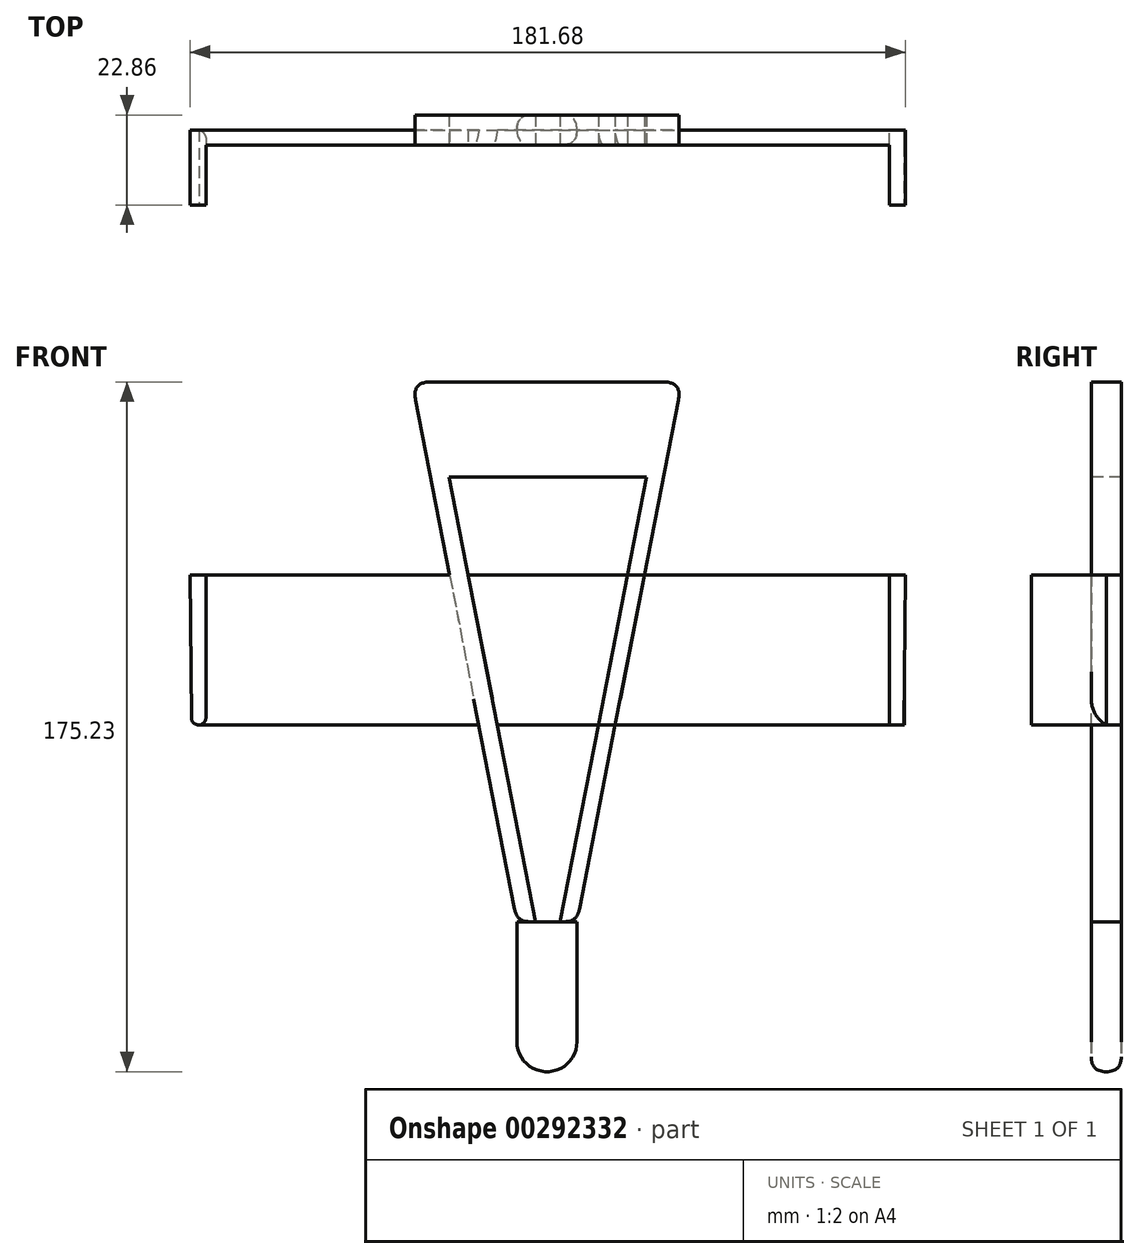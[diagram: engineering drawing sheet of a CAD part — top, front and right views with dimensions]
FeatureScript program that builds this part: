
annotation { "Feature Type Name" : "Feature", "Feature Type Description" : "" }
export const myFeature = defineFeature(function(context is Context, id is Id, definition is map)
    precondition{}
    {
        {
            var Q0;
            Q0=qCreatedBy(makeId("Front.planeOp"),FACE);
            var sketch = newSketch(context, id + "F0", { "sketchPlane" : qUnion([Q0])});
            skLineSegment(sketch, "E0", {"start": v(-7.81, -36.6) * mm, "end": v(7.43, -36.6) * mm});
            skLineSegment(sketch, "E1", {"start": v(7.43, -36.6) * mm, "end": v(7.43, -67.07) * mm});
            skLineSegment(sketch, "E2", {"start": v(-7.81, -36.6) * mm, "end": v(-7.81, -67.07) * mm});
            skArc(sketch, "E3", {"start": v(-7.81, -67.07) * mm, "mid": v(-0.2, -74.7) * mm, "end": v(7.43, -67.07) * mm});
            skLineSegment(sketch, "E4", {"start": v(7.43, -36.6) * mm, "end": v(34.07, 100.54) * mm});
            skLineSegment(sketch, "E5", {"start": v(34.07, 100.54) * mm, "end": v(-34.46, 100.54) * mm});
            skLineSegment(sketch, "E6", {"start": v(-34.46, 100.54) * mm, "end": v(-7.81, -36.6) * mm});
            skLineSegment(sketch, "E7", {"start": v(3.15, -36.6) * mm, "end": v(25.1, 76.38) * mm});
            skLineSegment(sketch, "E8", {"start": v(25.1, 76.38) * mm, "end": v(-25.04, 76.38) * mm});
            skLineSegment(sketch, "E9", {"start": v(-25.04, 76.38) * mm, "end": v(-3.1, -36.6) * mm});
            skLineSegment(sketch, "E10", {"start": v(-8.63, -8.1) * mm, "end": v(8.68, -8.1) * mm});
            skLineSegment(sketch, "E11", {"start": v(-11.11, 4.67) * mm, "end": v(11.16, 4.67) * mm});
            skLineSegment(sketch, "E12", {"start": v(-90.84, 51.55) * mm, "end": v(90.63, 51.55) * mm});
            skLineSegment(sketch, "E13", {"start": v(90.63, 51.55) * mm, "end": v(90.63, 13.38) * mm});
            skLineSegment(sketch, "E14", {"start": v(90.63, 13.38) * mm, "end": v(-90.52, 13.38) * mm});
            skLineSegment(sketch, "E15", {"start": v(-90.52, 13.38) * mm, "end": v(-90.84, 51.55) * mm});
            skSolve(sketch);
        }
        {
            var Q0;
            {var subQ0=sQuery(id+"F0.wireOp",EDGE,"E7");var subQ3=sQuery(id+"F0.wireOp",EDGE,"E0");var subQ4=makeQuery(id+"F0.imprint","INTERSECT",VERTEX,{"derivedFrom":[subQ3,subQ0]});Q0=makeQuery(id+"F0.imprint","IMPRINT",FACE,{"disambiguationData":[TD([[makeQuery(id+"F0.imprint","IMPRINT",EDGE,{"disambiguationData":[TD([[subQ4,-1.0]])],"derivedFrom":subQ0}),-1.0]])]});}
            var Q1;
            {var subQ5=sQuery(id+"F0.wireOp",EDGE,"E5");Q1=makeQuery(id+"F0.imprint","IMPRINT",FACE,{"disambiguationData":[TD([[makeQuery(id+"F0.imprint","IMPRINT",EDGE,{"derivedFrom":subQ5}),1.0]])]});}
            var Q2;
            {var subQ0=sQuery(id+"F0.wireOp",EDGE,"E9");var subQ1=makeQuery(id+"F0.imprint","INTERSECT",VERTEX,{"derivedFrom":[subQ0,sQuery(id+"F0.wireOp",EDGE,"E11")]});Q2=makeQuery(id+"F0.imprint","IMPRINT",FACE,{"disambiguationData":[TD([[makeQuery(id+"F0.imprint","IMPRINT",EDGE,{"disambiguationData":[TD([[subQ1,1.0]])],"derivedFrom":subQ0}),-1.0]])]});}
            extrude(context, id + "F1", {"entities" : qUnion([Q0, Q1, Q2]), "oppositeDirection" : true, "depth" : 7.62 * mm});
        }
        {
            var Q0;
            {var subQ0=sQuery(id+"F0.wireOp",EDGE,"E1");Q0=makeQuery(id+"F0.imprint","IMPRINT",FACE,{"disambiguationData":[TD([[makeQuery(id+"F0.imprint","IMPRINT",EDGE,{"derivedFrom":subQ0}),-1.0]])]});}
            extrude(context, id + "F2", {"entities" : qUnion([Q0]), "oppositeDirection" : true, "depth" : 7.62 * mm});
        }
        {
            var Q0;
            Q0=makeQuery(id+"F2.opExtrude","SWEPT_FACE",FACE,{"disambiguationData":[OSD([sQuery(id+"F0.wireOp",EDGE,"E3")])]});
            fillet(context, id + "F3", {"entities" : qUnion([Q0]), "radius" : 3.8 * mm, "tangentPropagation" : true, "rho" : 0.5, "crossSection" : FilletCrossSection.CONIC, "allowEdgeOverflow" : false});
        }
        {
            var Q0;
            {var subQ5=sQuery(id+"F0.wireOp",EDGE,"E13");Q0=makeQuery(id+"F0.imprint","IMPRINT",FACE,{"disambiguationData":[TD([[makeQuery(id+"F0.imprint","IMPRINT",EDGE,{"derivedFrom":subQ5}),-1.0]])]});}
            var Q1;
            {var subQ0=sQuery(id+"F0.wireOp",EDGE,"E14");var subQ1=sQuery(id+"F0.wireOp",EDGE,"E7");var subQ2=makeQuery(id+"F0.imprint","INTERSECT",VERTEX,{"derivedFrom":[subQ1,subQ0]});Q1=makeQuery(id+"F0.imprint","IMPRINT",FACE,{"disambiguationData":[TD([[makeQuery(id+"F0.imprint","IMPRINT",EDGE,{"disambiguationData":[TD([[subQ2,-1.0]])],"derivedFrom":subQ1}),1.0]])]});}
            var Q2;
            {var subQ5=sQuery(id+"F0.wireOp",EDGE,"E15");Q2=makeQuery(id+"F0.imprint","IMPRINT",FACE,{"disambiguationData":[TD([[makeQuery(id+"F0.imprint","IMPRINT",EDGE,{"derivedFrom":subQ5}),-1.0]])]});}
            extrude(context, id + "F4", {"entities" : qUnion([Q0, Q1, Q2]), "oppositeDirection" : true, "depth" : 3.8 * mm});
        }
        {
            var Q0;
            {var subQ0=sQuery(id+"F0.wireOp",EDGE,"E12");var subQ1=sQuery(id+"F0.wireOp",EDGE,"E6");var subQ2=makeQuery(id+"F0.imprint","INTERSECT",VERTEX,{"derivedFrom":[subQ1,subQ0]});Q0=makeQuery(id+"F0.imprint","IMPRINT",FACE,{"disambiguationData":[TD([[makeQuery(id+"F0.imprint","IMPRINT",EDGE,{"disambiguationData":[TD([[subQ2,-1.0]])],"derivedFrom":subQ1}),1.0]])]});}
            var Q1;
            {var subQ0=sQuery(id+"F0.wireOp",EDGE,"E14");var subQ1=sQuery(id+"F0.wireOp",EDGE,"E4");var subQ2=makeQuery(id+"F0.imprint","INTERSECT",VERTEX,{"derivedFrom":[subQ1,subQ0]});Q1=makeQuery(id+"F0.imprint","IMPRINT",FACE,{"disambiguationData":[TD([[makeQuery(id+"F0.imprint","IMPRINT",EDGE,{"disambiguationData":[TD([[subQ2,-1.0]])],"derivedFrom":subQ1}),1.0]])]});}
            extrude(context, id + "F5", {"entities" : qUnion([Q0, Q1]), "oppositeDirection" : true, "depth" : 7.62 * mm});
        }
        {
            var Q0;
            Q0=makeQuery(id+"F1.opExtrude","SWEPT_EDGE",EDGE,{"disambiguationData":[OSD([sQuery(id+"F0.wireOp",EDGE,"E4"),sQuery(id+"F0.wireOp",EDGE,"E5")])]});
            var Q1;
            Q1=makeQuery(id+"F1.opExtrude","SWEPT_EDGE",EDGE,{"disambiguationData":[OSD([sQuery(id+"F0.wireOp",EDGE,"E0"),sQuery(id+"F0.wireOp",EDGE,"E1"),sQuery(id+"F0.wireOp",EDGE,"E4")])]});
            var Q2;
            Q2=makeQuery(id+"F1.opExtrude","SWEPT_EDGE",EDGE,{"disambiguationData":[OSD([sQuery(id+"F0.wireOp",EDGE,"E0"),sQuery(id+"F0.wireOp",EDGE,"E2"),sQuery(id+"F0.wireOp",EDGE,"E6")])]});
            var Q3;
            Q3=makeQuery(id+"F1.opExtrude","SWEPT_EDGE",EDGE,{"disambiguationData":[OSD([sQuery(id+"F0.wireOp",EDGE,"E5"),sQuery(id+"F0.wireOp",EDGE,"E6")])]});
            fillet(context, id + "F6", {"entities" : qUnion([Q0, Q1, Q2, Q3]), "radius" : 3.8 * mm, "tangentPropagation" : true, "rho" : 0.5, "crossSection" : FilletCrossSection.CONIC, "allowEdgeOverflow" : false});
        }
        {
            var Q0;
            Q0=makeQuery(id+"F4.opExtrude","CAP_FACE",FACE,{"disambiguationData":[OSD([sQuery(id+"F0.wireOp",EDGE,"E6"),sQuery(id+"F0.wireOp",EDGE,"E12"),sQuery(id+"F0.wireOp",EDGE,"E14"),sQuery(id+"F0.wireOp",EDGE,"E15")])],"isStart":false});
            var sketch = newSketch(context, id + "F7", { "sketchPlane" : qUnion([Q0])});
            skLineSegment(sketch, "E16", {"start": v(86.83, 13.38) * mm, "end": v(86.83, 51.55) * mm});
            skLineSegment(sketch, "E17.MirrorCS", {"start": v(-86.83, 13.38) * mm, "end": v(-86.83, 51.55) * mm});
            skSolve(sketch);
        }
        {
            var Q0;
            {var subQ0=sQuery(id+"F7.wireOp",EDGE,"E16");Q0=makeQuery(id+"F7.imprint","IMPRINT",FACE,{"disambiguationData":[TD([[makeQuery(id+"F7.imprint","IMPRINT",EDGE,{"derivedFrom":subQ0}),-1.0]])]});}
            extrude(context, id + "F8", {"entities" : qUnion([Q0]), "operationType" : NewBodyOperationType.ADD, "oppositeDirection" : true, "depth" : 19.05 * mm});
        }
        {
            var Q0;
            Q0=makeQuery(id+"F4.opExtrude","SWEPT_BODY",BODY,{"disambiguationData":[OSD([sQuery(id+"F0.wireOp",EDGE,"E6"),sQuery(id+"F0.wireOp",EDGE,"E12"),sQuery(id+"F0.wireOp",EDGE,"E14"),sQuery(id+"F0.wireOp",EDGE,"E15")])]});
            var Q1;
            Q1=qCreatedBy(makeId("Right.planeOp"),FACE);
            mirror(context, id + "F9", {"operationType" : NewBodyOperationType.ADD, "entities" : qUnion([Q0]), "mirrorPlane" : qUnion([Q1])});
        }
        {
            var Q0;
            {var subQ0=sQuery(id+"F0.wireOp",EDGE,"E15");var subQ1=sQuery(id+"F0.wireOp",EDGE,"E14");Q0=makeQuery(id+"F8.boolean.opBoolean","MERGE",EDGE,{"derivedFrom":[makeQuery(id+"F4.opExtrude","SWEPT_EDGE",EDGE,{"disambiguationData":[OSD([subQ1,subQ0])]}),makeQuery(id+"F8.opExtrude","SWEPT_EDGE",EDGE,{"disambiguationData":[OSD([subQ1,subQ0])]})]});}
            fillet(context, id + "F10", {"entities" : qUnion([Q0]), "radius" : 1.9 * mm, "tangentPropagation" : true, "allowEdgeOverflow" : false});
        }
        {
            var Q0;
            Q0=makeQuery(id+"F8.opExtrude","SWEPT_EDGE",EDGE,{"disambiguationData":[OSD([sQuery(id+"F0.wireOp",EDGE,"E14"),sQuery(id+"F7.wireOp",EDGE,"E16")])]});
            fillet(context, id + "F11", {"entities" : qUnion([Q0]), "radius" : 1.9 * mm, "tangentPropagation" : true, "allowEdgeOverflow" : false});
        }
        {
            var Q0;
            {var subQ0=sQuery(id+"F0.wireOp",EDGE,"E14");Q0=makeQuery(id+"F4.opExtrude","CAP_EDGE",EDGE,{"disambiguationData":[OSD([subQ0]),TDD([makeQuery(id+"F0.imprint","IMPRINT",EDGE,{"disambiguationData":[TD([[makeQuery(id+"F0.imprint","INTERSECT",VERTEX,{"derivedFrom":[subQ0,sQuery(id+"F0.wireOp",EDGE,"E15")]}),1.0]])],"derivedFrom":subQ0})])],"isStart":true});}
            var Q1;
            {var subQ0=sQuery(id+"F0.wireOp",EDGE,"E14");var subQ1=sQuery(id+"F0.wireOp",EDGE,"E13");var subQ2=sQuery(id+"F0.wireOp",EDGE,"E4");var subQ3=makeQuery(id+"F4.opExtrude","CAP_FACE",FACE,{"disambiguationData":[OSD([subQ2,sQuery(id+"F0.wireOp",EDGE,"E12"),subQ1,subQ0])],"isStart":true});var subQ4=makeQuery(id+"F0.imprint","IMPRINT",EDGE,{"disambiguationData":[TD([[makeQuery(id+"F0.imprint","INTERSECT",VERTEX,{"derivedFrom":[subQ1,subQ0]}),-1.0]])],"derivedFrom":subQ0});var subQ5=makeQuery(id+"F4.opExtrude","SWEPT_FACE",FACE,{"disambiguationData":[OSD([subQ0]),TDD([subQ4])]});Q1=makeQuery(id+"F9.boolean.opBoolean","SPLIT",EDGE,{"disambiguationData":[topologyDisambiguationEdgeConnected([subQ3,subQ5]),TD([makeQuery(id+"F9.opPattern","COPY",FACE,{"derivedFrom":makeQuery(id+"F8.opExtrude","SWEPT_FACE",FACE,{"disambiguationData":[OSD([sQuery(id+"F7.wireOp",EDGE,"E16")])]}),"instanceName":"1"})])],"derivedFrom":makeQuery(id+"F4.opExtrude","CAP_EDGE",EDGE,{"disambiguationData":[OSD([subQ0]),TDD([subQ4])],"isStart":true})});}
            fillet(context, id + "F12", {"entities" : qUnion([Q0, Q1]), "radius" : 7.62 * mm, "tangentPropagation" : true, "allowEdgeOverflow" : false});
        }
        {
            var Q0;
            {var subQ0=sQuery(id+"F0.wireOp",EDGE,"E14");Q0=makeQuery(id+"F4.opExtrude","CAP_EDGE",EDGE,{"disambiguationData":[OSD([subQ0]),TDD([makeQuery(id+"F0.imprint","IMPRINT",EDGE,{"disambiguationData":[TD([[makeQuery(id+"F0.imprint","INTERSECT",VERTEX,{"derivedFrom":[sQuery(id+"F0.wireOp",EDGE,"E7"),subQ0]}),-1.0]])],"derivedFrom":subQ0})])],"isStart":true});}
            fillet(context, id + "F13", {"entities" : qUnion([Q0]), "radius" : 7.62 * mm, "tangentPropagation" : true, "allowEdgeOverflow" : false});
        }
    });
